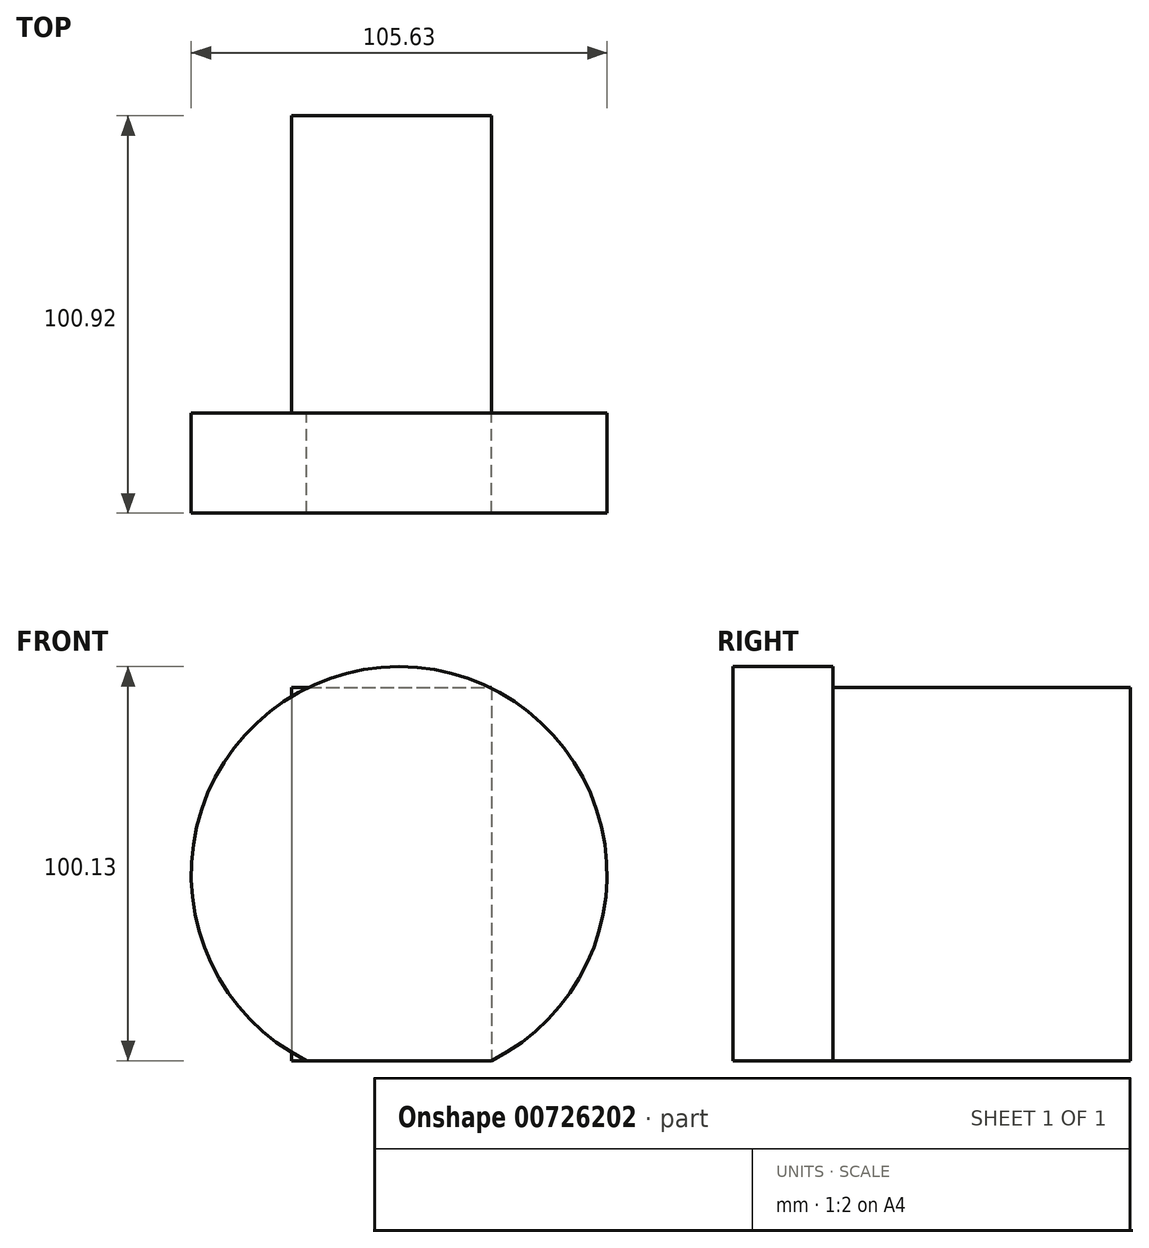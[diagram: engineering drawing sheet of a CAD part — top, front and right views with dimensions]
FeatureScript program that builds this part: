
annotation { "Feature Type Name" : "Feature", "Feature Type Description" : "" }
export const myFeature = defineFeature(function(context is Context, id is Id, definition is map)
    precondition{}
    {
        {
            var Q0;
            Q0=qCreatedBy(makeId("Front.planeOp"),FACE);
            var sketch = newSketch(context, id + "F0", { "sketchPlane" : qUnion([Q0])});
            skLineSegment(sketch, "E0", {"start": v(-65.09, 0) * mm, "end": v(52.54, 0) * mm});
            skLineSegment(sketch, "E1", {"start": v(52.54, 0) * mm, "end": v(52.54, 47.32) * mm});
            skCircle(sketch, "E2", {"center": v(-23.46, 47.32) * mm, "radius": 52.81 * mm});
            skSolve(sketch);
        }
        {
            var Q0;
            {var subQ0=sQuery(id+"F0.wireOp",EDGE,"E2");var subQ1=sQuery(id+"F0.wireOp",EDGE,"E0");var subQ2=makeQuery(id+"F0.imprint","INTERSECT",VERTEX,{"disambiguationData":[OD(0.0)],"derivedFrom":[subQ1,subQ0]});Q0=makeQuery(id+"F0.imprint","IMPRINT",FACE,{"disambiguationData":[TD([[makeQuery(id+"F0.imprint","IMPRINT",EDGE,{"disambiguationData":[TD([[subQ2,-1.0]])],"derivedFrom":subQ1}),1.0]])]});}
            extrude(context, id + "F1", {"entities" : qUnion([Q0]), "depth" : 25.4 * mm, "offsetDistance" : 25.4 * mm});
        }
        {
            var Q0;
            Q0=qCreatedBy(makeId("Right.planeOp"),FACE);
            var sketch = newSketch(context, id + "F2", { "sketchPlane" : qUnion([Q0])});
            skLineSegment(sketch, "E3.bottom", {"start": v(0, 94.78) * mm, "end": v(75.52, 94.78) * mm});
            skLineSegment(sketch, "E3.top", {"start": v(0, 0) * mm, "end": v(75.52, 0) * mm});
            skLineSegment(sketch, "E3.left", {"start": v(0, 94.78) * mm, "end": v(0, 0) * mm});
            skLineSegment(sketch, "E3.right", {"start": v(75.52, 94.78) * mm, "end": v(75.52, 0) * mm});
            skSolve(sketch);
        }
        {
            var Q0;
            Q0=makeQuery(id+"F2.imprint","IMPRINT",FACE,{"disambiguationData":[TD([[makeQuery(id+"F2.imprint","IMPRINT",EDGE,{"derivedFrom":sQuery(id+"F2.wireOp",EDGE,"E3.bottom")}),-1.0]])]});
            extrude(context, id + "F3", {"entities" : qUnion([Q0]), "operationType" : NewBodyOperationType.ADD, "oppositeDirection" : true, "depth" : 50.8 * mm, "offsetDistance" : 25.4 * mm});
        }
    });
